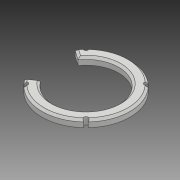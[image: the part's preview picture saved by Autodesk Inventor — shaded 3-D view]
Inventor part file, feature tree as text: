
AUTODESK INVENTOR PART (.ipt)
format: ipt  version: 2018 (Build 220112000, 112)  size: 263,680 bytes
history: native  units: mm
features: other x4, reference x4, extrude x2, sketch x2, chamfer x1
ambient origin geometry x8: Origin, YZ Plane, XZ Plane, XY Plane, X Axis, Y Axis, Z Axis, Center Point
bodies: Body1 (feature_tree)
feature tree (13):
  other  "ソリッド1"
  extrude  "押し出し1"  Depth=23.0mm
  chamfer  "面取り1"  Distance=8.0mm
  extrude  "押し出し2"  Depth=50.614548mm
  sketch  "スケッチ1"
  sketch  "スケッチ2"
  reference  "参照1"
  reference  "参照2"
  reference  "参照3"
  reference  "参照4"
  parser-record x1  (decoder bookkeeping rows leaked as tree rows — omitted from the tree; the rows remain in map.json)
  other  "topassy.iam"
  other  "topcover:1"
note: 1 file-system path scrubbed to <path> (originals preserved in map.json)
